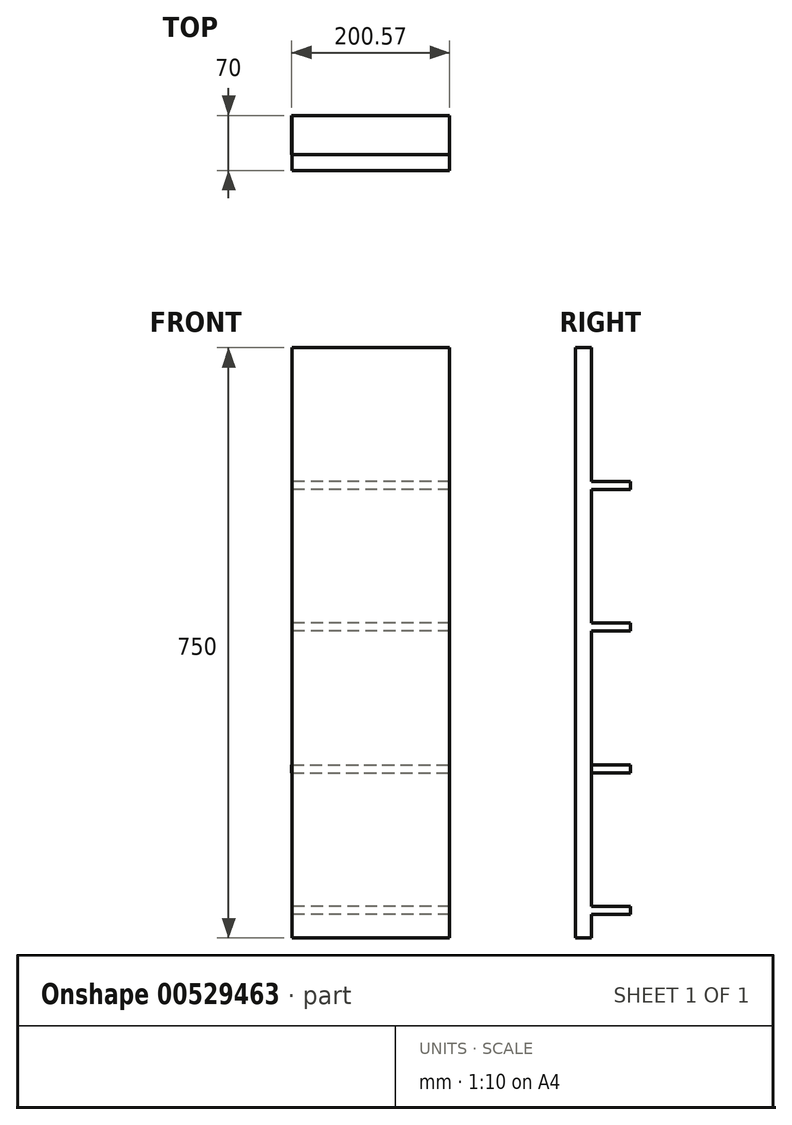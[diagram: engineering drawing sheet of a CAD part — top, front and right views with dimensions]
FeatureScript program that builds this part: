
annotation { "Feature Type Name" : "Feature", "Feature Type Description" : "" }
export const myFeature = defineFeature(function(context is Context, id is Id, definition is map)
    precondition{}
    {
        {
            var Q0;
            Q0=qCreatedBy(makeId("Front.planeOp"),FACE);
            var sketch = newSketch(context, id + "F0", { "sketchPlane" : qUnion([Q0])});
            skLineSegment(sketch, "E0.bottom", {"start": v(-317.5, 434.85) * mm, "end": v(-117.5, 434.85) * mm});
            skLineSegment(sketch, "E0.top", {"start": v(-317.5, -315.15) * mm, "end": v(-117.5, -315.15) * mm});
            skLineSegment(sketch, "E0.left", {"start": v(-317.5, 434.85) * mm, "end": v(-317.5, -315.15) * mm});
            skLineSegment(sketch, "E0.right", {"start": v(-117.5, 434.85) * mm, "end": v(-117.5, -315.15) * mm});
            skSolve(sketch);
        }
        {
            var Q0;
            Q0=makeQuery(id+"F0.imprint","IMPRINT",FACE,{"disambiguationData":[TD([[makeQuery(id+"F0.imprint","IMPRINT",EDGE,{"derivedFrom":sQuery(id+"F0.wireOp",EDGE,"E0.bottom")}),-1.0]])]});
            extrude(context, id + "F1", {"entities" : qUnion([Q0]), "depth" : 20 * mm, "offsetDistance" : 25.4 * mm});
        }
        {
            var Q0;
            Q0=qCreatedBy(makeId("Front.planeOp"),FACE);
            var sketch = newSketch(context, id + "F2", { "sketchPlane" : qUnion([Q0])});
            skLineSegment(sketch, "E1.bottom", {"start": v(-318.07, -105.15) * mm, "end": v(-118.07, -105.15) * mm});
            skLineSegment(sketch, "E1.top", {"start": v(-318.07, -95.15) * mm, "end": v(-118.07, -95.15) * mm});
            skLineSegment(sketch, "E1.left", {"start": v(-318.07, -105.15) * mm, "end": v(-318.07, -95.15) * mm});
            skLineSegment(sketch, "E1.right", {"start": v(-118.07, -105.15) * mm, "end": v(-118.07, -95.15) * mm});
            skPoint(sketch, "E1.middle", {"position": v(-218.07, -100.15) * mm});
            skSolve(sketch);
        }
        {
            var Q0;
            Q0=makeQuery(id+"F2.imprint","IMPRINT",FACE,{"disambiguationData":[TD([[makeQuery(id+"F2.imprint","IMPRINT",EDGE,{"derivedFrom":sQuery(id+"F2.wireOp",EDGE,"E1.bottom")}),1.0]])]});
            extrude(context, id + "F3", {"entities" : qUnion([Q0]), "operationType" : NewBodyOperationType.ADD, "oppositeDirection" : true, "depth" : 50 * mm, "offsetDistance" : 25.4 * mm});
        }
        {
            var Q0;
            Q0=qCreatedBy(makeId("Front.planeOp"),FACE);
            var sketch = newSketch(context, id + "F4", { "sketchPlane" : qUnion([Q0])});
            skLineSegment(sketch, "E2.bottom", {"start": v(-117.5, 84.85) * mm, "end": v(-317.5, 84.85) * mm});
            skLineSegment(sketch, "E2.top", {"start": v(-117.5, 74.85) * mm, "end": v(-317.5, 74.85) * mm});
            skLineSegment(sketch, "E2.left", {"start": v(-117.5, 84.85) * mm, "end": v(-117.5, 74.85) * mm});
            skLineSegment(sketch, "E2.right", {"start": v(-317.5, 84.85) * mm, "end": v(-317.5, 74.85) * mm});
            skSolve(sketch);
        }
        {
            var Q0;
            Q0 = qSketchRegion(id + "F4", true);
            extrude(context, id + "F5", {"entities" : qUnion([Q0]), "operationType" : NewBodyOperationType.ADD, "oppositeDirection" : true, "depth" : 50 * mm, "offsetDistance" : 25.4 * mm});
        }
        {
            var Q0;
            Q0=qCreatedBy(makeId("Front.planeOp"),FACE);
            var sketch = newSketch(context, id + "F6", { "sketchPlane" : qUnion([Q0])});
            skLineSegment(sketch, "E3.bottom", {"start": v(-117.5, 264.85) * mm, "end": v(-317.5, 264.85) * mm});
            skLineSegment(sketch, "E3.top", {"start": v(-117.5, 254.85) * mm, "end": v(-317.5, 254.85) * mm});
            skLineSegment(sketch, "E3.left", {"start": v(-117.5, 264.85) * mm, "end": v(-117.5, 254.85) * mm});
            skLineSegment(sketch, "E3.right", {"start": v(-317.5, 264.85) * mm, "end": v(-317.5, 254.85) * mm});
            skSolve(sketch);
        }
        {
            var Q0;
            Q0 = qSketchRegion(id + "F6", true);
            extrude(context, id + "F7", {"entities" : qUnion([Q0]), "operationType" : NewBodyOperationType.ADD, "oppositeDirection" : true, "depth" : 50 * mm, "offsetDistance" : 25.4 * mm});
        }
        {
            var Q0;
            Q0=qCreatedBy(makeId("Front.planeOp"),FACE);
            var sketch = newSketch(context, id + "F8", { "sketchPlane" : qUnion([Q0])});
            skLineSegment(sketch, "E4.bottom", {"start": v(-117.5, -275.15) * mm, "end": v(-317.5, -275.15) * mm});
            skLineSegment(sketch, "E4.top", {"start": v(-117.5, -285.15) * mm, "end": v(-317.5, -285.15) * mm});
            skLineSegment(sketch, "E4.left", {"start": v(-117.5, -275.15) * mm, "end": v(-117.5, -285.15) * mm});
            skLineSegment(sketch, "E4.right", {"start": v(-317.5, -275.15) * mm, "end": v(-317.5, -285.15) * mm});
            skSolve(sketch);
        }
        {
            var Q0;
            Q0 = qSketchRegion(id + "F8", true);
            extrude(context, id + "F9", {"entities" : qUnion([Q0]), "operationType" : NewBodyOperationType.ADD, "oppositeDirection" : true, "depth" : 50 * mm, "offsetDistance" : 25.4 * mm});
        }
    });
